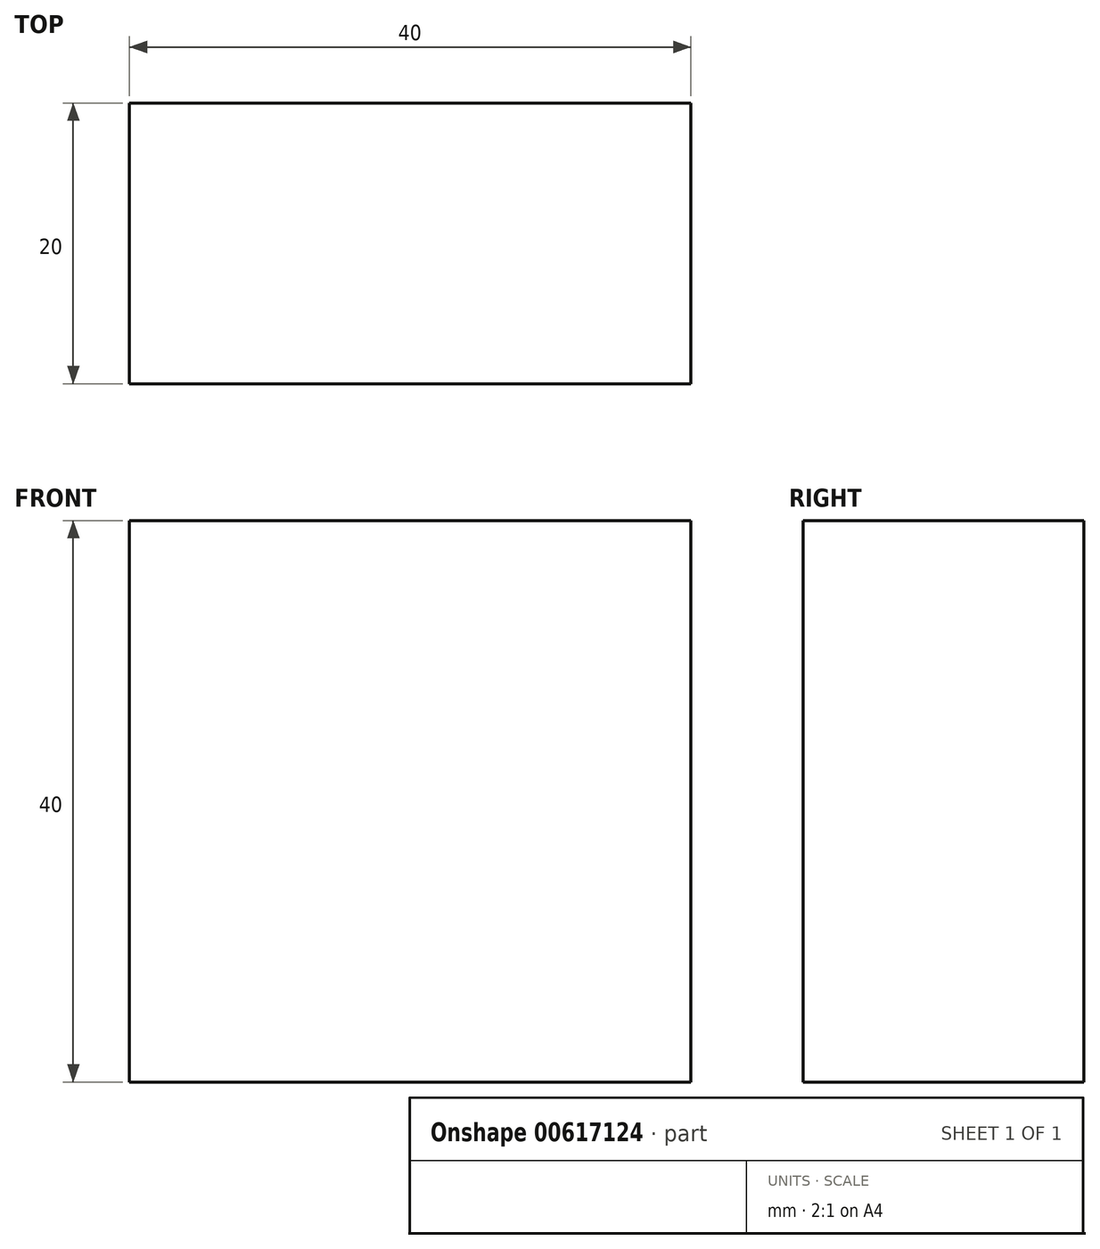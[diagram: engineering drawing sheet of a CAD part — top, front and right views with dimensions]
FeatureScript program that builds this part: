
annotation { "Feature Type Name" : "Feature", "Feature Type Description" : "" }
export const myFeature = defineFeature(function(context is Context, id is Id, definition is map)
    precondition{}
    {
        {
            var Q0;
            Q0=qCreatedBy(makeId("Front.planeOp"),FACE);
            var sketch = newSketch(context, id + "F0", { "sketchPlane" : qUnion([Q0])});
            skLineSegment(sketch, "E0", {"start": v(-40, 40) * mm, "end": v(0, 40) * mm});
            skLineSegment(sketch, "E1", {"start": v(0, 40) * mm, "end": v(0, 0) * mm});
            skLineSegment(sketch, "E2", {"start": v(-40, 40) * mm, "end": v(-40, 0) * mm});
            skLineSegment(sketch, "E3", {"start": v(-40, 0) * mm, "end": v(0, 0) * mm});
            skSolve(sketch);
        }
        {
            var Q0;
            Q0 = qSketchRegion(id + "F0", true);
            extrude(context, id + "F1", {"entities" : qUnion([Q0]), "depth" : 20 * mm, "offsetDistance" : 25 * mm});
        }
    });
